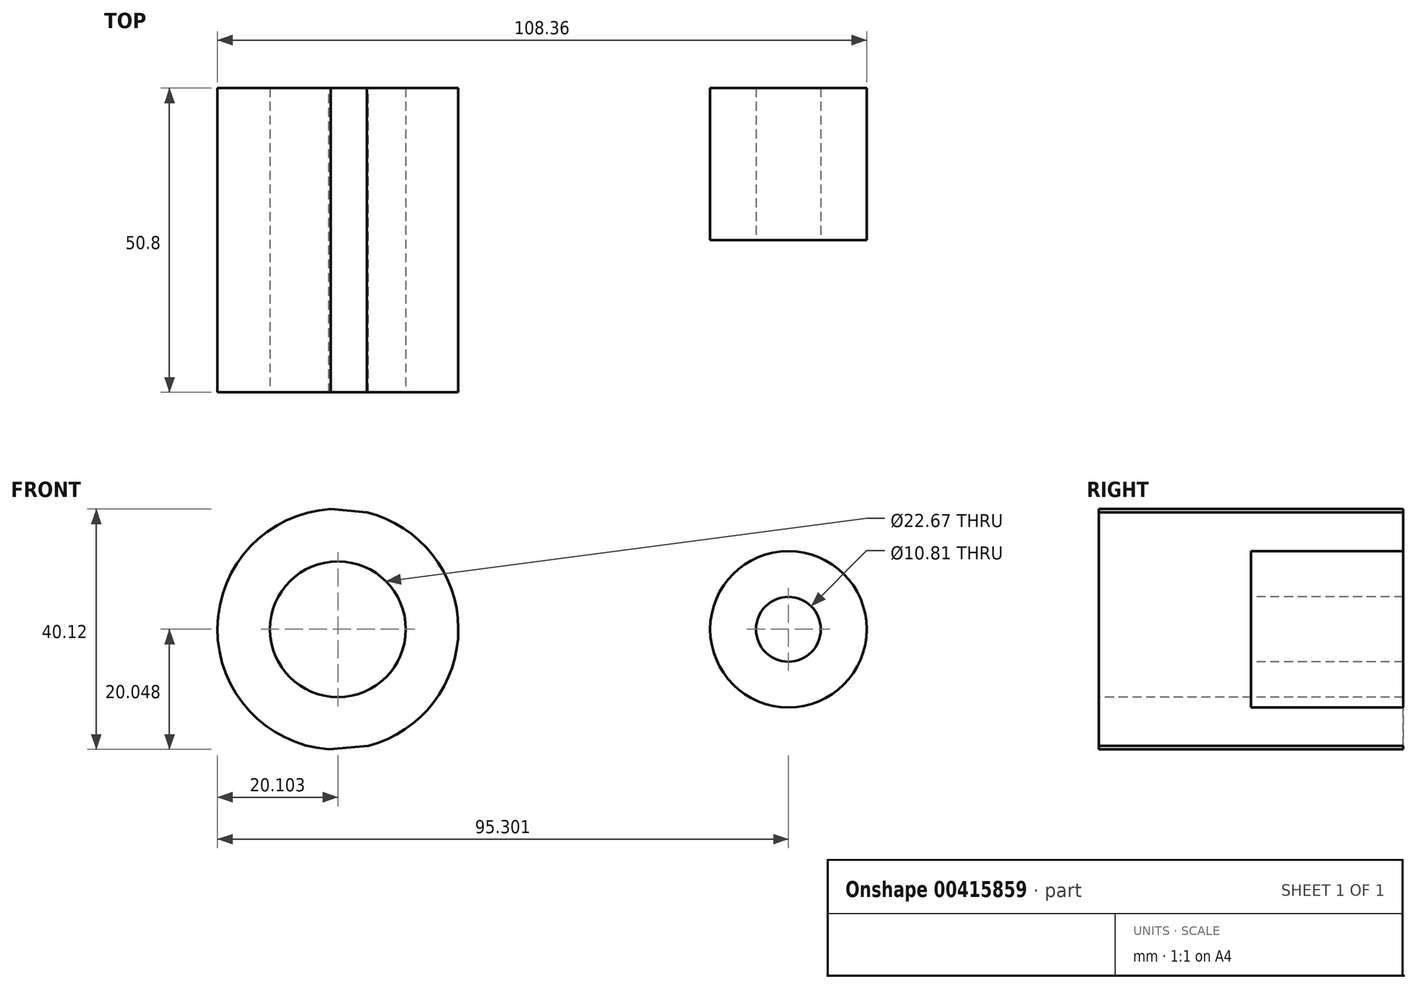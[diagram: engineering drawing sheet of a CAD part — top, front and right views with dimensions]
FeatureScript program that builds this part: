
annotation { "Feature Type Name" : "Feature", "Feature Type Description" : "" }
export const myFeature = defineFeature(function(context is Context, id is Id, definition is map)
    precondition{}
    {
        {
            var Q0;
            Q0=qCreatedBy(makeId("Front.planeOp"),FACE);
            var sketch = newSketch(context, id + "F0", { "sketchPlane" : qUnion([Q0])});
            skCircle(sketch, "E0", {"center": v(-63.47, 41.2) * mm, "radius": 20.1 * mm});
            skCircle(sketch, "E1", {"center": v(-63.47, 41.2) * mm, "radius": 12.21 * mm});
            skCircle(sketch, "E2", {"center": v(11.73, 41.2) * mm, "radius": 13.06 * mm});
            skCircle(sketch, "E3", {"center": v(11.73, 41.2) * mm, "radius": 5.79 * mm});
            skLineSegment(sketch, "E4", {"start": v(-64.67, 61.28) * mm, "end": v(12.92, 54.21) * mm});
            skLineSegment(sketch, "E5", {"start": v(-65, 21.16) * mm, "end": v(12.9, 28.2) * mm});
            skSolve(sketch);
        }
        {
            var Q0;
            {var subQ0=sQuery(id+"F0.wireOp",EDGE,"E4");var subQ1=sQuery(id+"F0.wireOp",EDGE,"E0");var subQ2=makeQuery(id+"F0.imprint","INTERSECT",VERTEX,{"disambiguationData":[OD(1.0)],"derivedFrom":[subQ1,subQ0]});Q0=makeQuery(id+"F0.imprint","IMPRINT",FACE,{"disambiguationData":[TD([[makeQuery(id+"F0.imprint","IMPRINT",EDGE,{"disambiguationData":[TD([[subQ2,1.0]])],"derivedFrom":subQ1}),-1.0]])]});}
            var Q1;
            Q1=makeQuery(id+"F0.imprint","IMPRINT",FACE,{"disambiguationData":[TD([[makeQuery(id+"F0.imprint","IMPRINT",EDGE,{"derivedFrom":sQuery(id+"F0.wireOp",EDGE,"E3")}),-1.0]])]});
            var Q2;
            {var subQ0=sQuery(id+"F0.wireOp",EDGE,"E4");var subQ1=sQuery(id+"F0.wireOp",EDGE,"E0");var subQ2=makeQuery(id+"F0.imprint","INTERSECT",VERTEX,{"disambiguationData":[OD(0.0)],"derivedFrom":[subQ1,subQ0]});Q2=makeQuery(id+"F0.imprint","IMPRINT",FACE,{"disambiguationData":[TD([[makeQuery(id+"F0.imprint","IMPRINT",EDGE,{"disambiguationData":[TD([[subQ2,1.0]])],"derivedFrom":subQ1}),1.0]])]});}
            var Q3;
            {var subQ0=sQuery(id+"F0.wireOp",EDGE,"E5");var subQ1=sQuery(id+"F0.wireOp",EDGE,"E0");var subQ2=makeQuery(id+"F0.imprint","INTERSECT",VERTEX,{"disambiguationData":[OD(0.0)],"derivedFrom":[subQ1,subQ0]});Q3=makeQuery(id+"F0.imprint","IMPRINT",FACE,{"disambiguationData":[TD([[makeQuery(id+"F0.imprint","IMPRINT",EDGE,{"disambiguationData":[TD([[subQ2,-1.0]])],"derivedFrom":subQ1}),1.0]])]});}
            var Q4;
            Q4=makeQuery(id+"F0.imprint","IMPRINT",FACE,{"disambiguationData":[TD([[makeQuery(id+"F0.imprint","IMPRINT",EDGE,{"derivedFrom":sQuery(id+"F0.wireOp",EDGE,"E3")}),1.0]])]});
            var Q5;
            Q5=makeQuery(id+"F0.imprint","IMPRINT",FACE,{"disambiguationData":[TD([[makeQuery(id+"F0.imprint","IMPRINT",EDGE,{"derivedFrom":sQuery(id+"F0.wireOp",EDGE,"E1")}),-1.0]])]});
            var Q6;
            Q6=makeQuery(id+"F0.imprint","IMPRINT",FACE,{"disambiguationData":[TD([[makeQuery(id+"F0.imprint","IMPRINT",EDGE,{"derivedFrom":sQuery(id+"F0.wireOp",EDGE,"E1")}),1.0]])]});
            extrude(context, id + "F1", {"entities" : qUnion([Q0, Q1, Q2, Q3, Q4, Q5, Q6]), "depth" : 25.4 * mm, "hasSecondDirectionDraft" : true, "secondDirectionDraftAngle" : 3 * degree});
        }
        {
            var Q0;
            Q0=qCreatedBy(makeId("Front.planeOp"),FACE);
            var sketch = newSketch(context, id + "F2", { "sketchPlane" : qUnion([Q0])});
            skCircle(sketch, "E6", {"center": v(-100.2, -20.05) * mm, "radius": 6.35 * mm});
            skSolve(sketch);
        }
        {
            var Q0;
            Q0=makeQuery(id+"F2.imprint","IMPRINT",FACE,{"disambiguationData":[TD([[makeQuery(id+"F2.imprint","IMPRINT",EDGE,{"derivedFrom":sQuery(id+"F2.wireOp",EDGE,"E6")}),1.0]])]});
            extrude(context, id + "F3", {"entities" : qUnion([Q0]), "depth" : 25.4 * mm});
        }
        {
            var Q0;
            Q0=makeQuery(id+"F1.opExtrude","CAP_FACE",FACE,{"disambiguationData":[OSD([sQuery(id+"F0.wireOp",EDGE,"E0"),sQuery(id+"F0.wireOp",EDGE,"E2"),sQuery(id+"F0.wireOp",EDGE,"E4"),sQuery(id+"F0.wireOp",EDGE,"E5")])],"isStart":false});
            extrude(context, id + "F4", {"entities" : qUnion([Q0]), "operationType" : NewBodyOperationType.ADD, "depth" : 25.4 * mm});
        }
        {
            var Q0;
            Q0=makeQuery(id+"F4.opExtrude","CAP_FACE",FACE,{"disambiguationData":[OSD([sQuery(id+"F0.wireOp",EDGE,"E0"),sQuery(id+"F0.wireOp",EDGE,"E2"),sQuery(id+"F0.wireOp",EDGE,"E4"),sQuery(id+"F0.wireOp",EDGE,"E5")])],"isStart":false});
            var sketch = newSketch(context, id + "F5", { "sketchPlane" : qUnion([Q0])});
            skCircle(sketch, "E7", {"center": v(-63.47, 41.2) * mm, "radius": 11.34 * mm});
            skCircle(sketch, "E8", {"center": v(11.73, 41.2) * mm, "radius": 5.4 * mm});
            skSolve(sketch);
        }
        {
            var Q0;
            Q0=makeQuery(id+"F5.imprint","IMPRINT",FACE,{"disambiguationData":[TD([[makeQuery(id+"F5.imprint","IMPRINT",EDGE,{"derivedFrom":sQuery(id+"F5.wireOp",EDGE,"E7")}),1.0]])]});
            var Q1;
            Q1=makeQuery(id+"F5.imprint","IMPRINT",FACE,{"disambiguationData":[TD([[makeQuery(id+"F5.imprint","IMPRINT",EDGE,{"derivedFrom":sQuery(id+"F5.wireOp",EDGE,"E8")}),1.0]])]});
            extrude(context, id + "F6", {"entities" : qUnion([Q0, Q1]), "operationType" : NewBodyOperationType.REMOVE, "oppositeDirection" : true, "depth" : 143.76 * mm});
        }
        {
            var Q0;
            Q0=makeQuery(id+"F3.opExtrude","SWEPT_BODY",BODY,{"disambiguationData":[OSD([sQuery(id+"F2.wireOp",EDGE,"E6")])]});
            deleteBodies(context, id + "F7", {"entities" : qUnion([Q0])});
        }
    });
